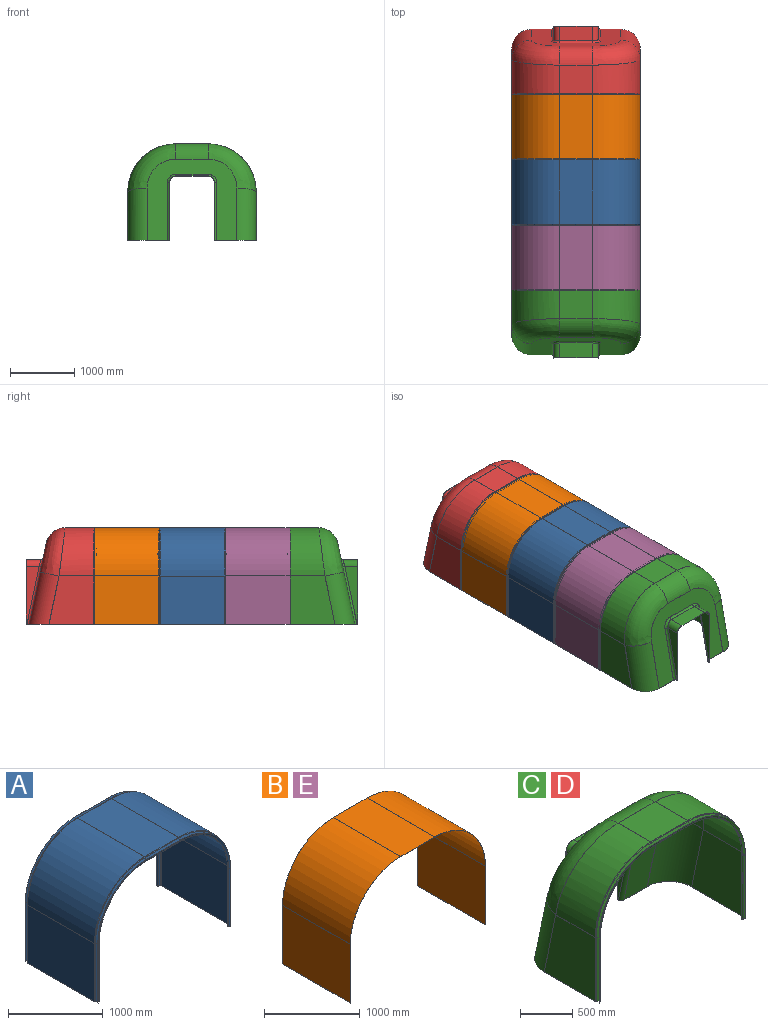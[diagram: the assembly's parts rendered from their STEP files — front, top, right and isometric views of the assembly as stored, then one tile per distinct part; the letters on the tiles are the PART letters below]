
ASSEMBLY  parts=5 mates=4
PART A: 102 faces, bbox 2123.6x1086.8x1561.8 mm
  f0: plane 1086.76x38mm, normal (0,0,-1), area 2320.8mm2, adj f3,f7,f12,f13,f14,f15,f16,f17
  f1: plane 1000x750mm, normal (-1,0,0), area 750000mm2, adj f2,f6,f52,f93
  f2: plane 1086.76x38mm, normal (0,0,-1), area 2320.8mm2, adj f1,f11,f48,f49,f50,f51,f52,f53
  f3: plane 1000x750mm, normal (1,0,0), area 750000mm2, adj f0,f5,f16,f57
  f4: plane 1000x500mm, normal (0,0,1), area 500000mm2, adj f5,f6,f34,f75
  f5: cylinder r=750mm len=1000mm, axis (0,1,0), area 1178097.2mm2, adj f3,f4,f25,f66
  f6: cylinder r=750mm len=1000mm, axis (0,-1,0), area 1178097.2mm2, adj f1,f4,f43,f84
  f7: plane 1000x750mm, normal (-1,0,0), area 750000mm2, adj f0,f8,f17,f65
  f8: cylinder r=748mm len=1000mm, axis (0,-1,0), area 1174955.7mm2, adj f7,f9,f26,f74
  f9: plane 1000x500mm, normal (0,0,-1), area 500000mm2, adj f8,f10,f35,f83
  f10: cylinder r=748mm len=1000mm, axis (0,-1,0), area 1174955.7mm2, adj f9,f11,f44,f92
  f11: plane 1000x750mm, normal (1,0,0), area 750000mm2, adj f2,f10,f53,f101
  f12: plane 750x1.84mm, normal (0.92,-0.39,0), area 1500mm2, adj f0,f13,f20,f21
  f13: plane 750x21.74mm, normal (0.39,0.92,0), area 17709.1mm2, adj f0,f12,f14,f22
  f14: cylinder r=7mm len=750mm, axis (0,0,1), area 12278.4mm2, adj f0,f13,f15,f23
  f15: plane 750x26.25mm, normal (0.39,-0.92,0), area 21389.1mm2, adj f0,f14,f16,f24
  f16: cylinder r=9mm len=750mm, axis (0,0,1), area 7893.3mm2, adj f0,f3,f15,f25
  f17: cylinder r=7mm len=750mm, axis (0,0,1), area 6139.2mm2, adj f0,f7,f18,f26
  f18: plane 750x26.25mm, normal (-0.39,0.92,0), area 21389.1mm2, adj f0,f17,f19,f27
  f19: cylinder r=9mm len=750mm, axis (0,0,1), area 15786.5mm2, adj f0,f18,f20,f28
  f20: plane 750x21.74mm, normal (-0.39,-0.92,0), area 17709.1mm2, adj f0,f12,f19,f29
  f21: cone r=739.22mm half-angle=23deg, axis (0,1,0), area 2323.6mm2, adj f12,f22,f29,f30
  f22: cone r=740mm half-angle=67deg, axis (0,-1,0), area 27043.5mm2, adj f13,f21,f23,f31
  f23: torus R=721mm, axis (0,-1,0), area 18399.4mm2, adj f14,f22,f24,f32
  f24: cone r=718.26mm half-angle=67deg, axis (0,1,0), area 32764.3mm2, adj f15,f23,f25,f33
  f25: torus R=741mm, axis (0,-1,0), area 12367mm2, adj f5,f16,f24,f34
  f26: torus R=741mm, axis (0,-1,0), area 9598.6mm2, adj f8,f17,f27,f35
  f27: cone r=743.74mm half-angle=67deg, axis (0,1,0), area 32729.3mm2, adj f18,f26,f28,f36
  f28: torus R=721mm, axis (0,-1,0), area 23604.3mm2, adj f19,f27,f29,f37
  f29: cone r=717.48mm half-angle=67deg, axis (0,-1,0), area 27014.5mm2, adj f20,f21,f28,f38
  f30: plane 500x1.84mm, normal (0,-0.39,0.92), area 1000mm2, adj f21,f31,f38,f39
  f31: plane 500x21.74mm, normal (0,0.92,0.39), area 11806.1mm2, adj f22,f30,f32,f40
  f32: cylinder r=7mm len=500mm, axis (-1,0,0), area 8185.6mm2, adj f23,f31,f33,f41
  f33: plane 500x26.25mm, normal (0,-0.92,0.39), area 14259.4mm2, adj f24,f32,f34,f42
  f34: cylinder r=9mm len=500mm, axis (-1,0,0), area 5262.2mm2, adj f4,f25,f33,f43
  f35: cylinder r=7mm len=500mm, axis (-1,0,0), area 4092.8mm2, adj f9,f26,f36,f44
  f36: plane 500x26.25mm, normal (0,0.92,-0.39), area 14259.4mm2, adj f27,f35,f37,f45
  f37: cylinder r=9mm len=500mm, axis (-1,0,0), area 10524.3mm2, adj f28,f36,f38,f46
  f38: plane 500x21.74mm, normal (0,-0.92,-0.39), area 11806.1mm2, adj f29,f30,f37,f47
  f39: cone r=739.22mm half-angle=23deg, axis (0,1,0), area 2323.6mm2, adj f30,f40,f47,f48
  f40: cone r=740mm half-angle=67deg, axis (0,-1,0), area 27043.5mm2, adj f31,f39,f41,f49
  f41: torus R=721mm, axis (0,-1,0), area 18399.4mm2, adj f32,f40,f42,f50
  f42: cone r=718.26mm half-angle=67deg, axis (0,1,0), area 32764.3mm2, adj f33,f41,f43,f51
  f43: torus R=741mm, axis (0,-1,0), area 12367mm2, adj f6,f34,f42,f52
  f44: torus R=741mm, axis (0,-1,0), area 9598.6mm2, adj f10,f35,f45,f53
  f45: cone r=743.74mm half-angle=67deg, axis (0,1,0), area 32729.3mm2, adj f36,f44,f46,f54
  f46: torus R=721mm, axis (0,-1,0), area 23604.3mm2, adj f37,f45,f47,f55
  f47: cone r=717.48mm half-angle=67deg, axis (0,-1,0), area 27014.5mm2, adj f38,f39,f46,f56
  f48: plane 750x1.84mm, normal (-0.92,-0.39,0), area 1500mm2, adj f2,f39,f49,f56
  f49: plane 750x21.74mm, normal (-0.39,0.92,0), area 17709.1mm2, adj f2,f40,f48,f50
  f50: cylinder r=7mm len=750mm, axis (0,0,-1), area 12278.4mm2, adj f2,f41,f49,f51
  f51: plane 750x26.25mm, normal (-0.39,-0.92,0), area 21389.1mm2, adj f2,f42,f50,f52
  f52: cylinder r=9mm len=750mm, axis (0,0,-1), area 7893.3mm2, adj f1,f2,f43,f51
  f53: cylinder r=7mm len=750mm, axis (0,0,-1), area 6139.2mm2, adj f2,f11,f44,f54
  f54: plane 750x26.25mm, normal (0.39,0.92,0), area 21389.1mm2, adj f2,f45,f53,f55
  f55: cylinder r=9mm len=750mm, axis (0,0,-1), area 15786.5mm2, adj f2,f46,f54,f56
  f56: plane 750x21.74mm, normal (0.39,-0.92,0), area 17709.1mm2, adj f2,f47,f48,f55
  f57: cylinder r=9mm len=750mm, axis (0,0,1), area 7893.3mm2, adj f0,f3,f58,f66
  f58: plane 750x26.25mm, normal (0.39,0.92,0), area 21389.1mm2, adj f0,f57,f59,f67
  f59: cylinder r=7mm len=750mm, axis (0,0,1), area 12278.4mm2, adj f0,f58,f60,f68
  f60: plane 750x21.74mm, normal (0.39,-0.92,0), area 17709.1mm2, adj f0,f59,f61,f69
  f61: plane 750x1.84mm, normal (0.92,0.39,0), area 1500mm2, adj f0,f60,f62,f70
  f62: plane 750x21.74mm, normal (-0.39,0.92,0), area 17709.1mm2, adj f0,f61,f63,f71
  f63: cylinder r=9mm len=750mm, axis (0,0,1), area 15786.5mm2, adj f0,f62,f64,f72
  f64: plane 750x26.25mm, normal (-0.39,-0.92,0), area 21389.1mm2, adj f0,f63,f65,f73
  f65: cylinder r=7mm len=750mm, axis (0,0,1), area 6139.2mm2, adj f0,f7,f64,f74
  f66: torus R=741mm, axis (0,-1,0), area 12367mm2, adj f5,f57,f67,f75
  f67: cone r=744.52mm half-angle=67deg, axis (0,-1,0), area 32764.3mm2, adj f58,f66,f68,f76
  f68: torus R=721mm, axis (0,-1,0), area 18399.4mm2, adj f59,f67,f69,f77
  f69: cone r=718.26mm half-angle=67deg, axis (0,1,0), area 27043.5mm2, adj f60,f68,f70,f78
  f70: cone r=740mm half-angle=23deg, axis (0,-1,0), area 2323.6mm2, adj f61,f69,f71,f79
  f71: cone r=739.22mm half-angle=67deg, axis (0,1,0), area 27014.5mm2, adj f62,f70,f72,f80
  f72: torus R=721mm, axis (0,-1,0), area 23604.3mm2, adj f63,f71,f73,f81
  f73: cone r=717.48mm half-angle=67deg, axis (0,-1,0), area 32729.3mm2, adj f64,f72,f74,f82
  f74: torus R=741mm, axis (0,-1,0), area 9598.6mm2, adj f8,f65,f73,f83
  f75: cylinder r=9mm len=500mm, axis (-1,0,0), area 5262.2mm2, adj f4,f66,f76,f84
  f76: plane 500x26.25mm, normal (0,0.92,0.39), area 14259.4mm2, adj f67,f75,f77,f85
  f77: cylinder r=7mm len=500mm, axis (-1,0,0), area 8185.6mm2, adj f68,f76,f78,f86
  f78: plane 500x21.74mm, normal (0,-0.92,0.39), area 11806.1mm2, adj f69,f77,f79,f87
  f79: plane 500x1.84mm, normal (0,0.39,0.92), area 1000mm2, adj f70,f78,f80,f88
  f80: plane 500x21.74mm, normal (0,0.92,-0.39), area 11806.1mm2, adj f71,f79,f81,f89
  f81: cylinder r=9mm len=500mm, axis (-1,0,0), area 10524.3mm2, adj f72,f80,f82,f90
  f82: plane 500x26.25mm, normal (0,-0.92,-0.39), area 14259.4mm2, adj f73,f81,f83,f91
  f83: cylinder r=7mm len=500mm, axis (-1,0,0), area 4092.8mm2, adj f9,f74,f82,f92
  f84: torus R=741mm, axis (0,-1,0), area 12367mm2, adj f6,f75,f85,f93
  f85: cone r=744.52mm half-angle=67deg, axis (0,-1,0), area 32764.3mm2, adj f76,f84,f86,f94
  f86: torus R=721mm, axis (0,-1,0), area 18399.4mm2, adj f77,f85,f87,f95
  f87: cone r=718.26mm half-angle=67deg, axis (0,1,0), area 27043.5mm2, adj f78,f86,f88,f96
  f88: cone r=740mm half-angle=23deg, axis (0,-1,0), area 2323.6mm2, adj f79,f87,f89,f97
  f89: cone r=739.22mm half-angle=67deg, axis (0,1,0), area 27014.5mm2, adj f80,f88,f90,f98
  f90: torus R=721mm, axis (0,-1,0), area 23604.3mm2, adj f81,f89,f91,f99
  f91: cone r=717.48mm half-angle=67deg, axis (0,-1,0), area 32729.3mm2, adj f82,f90,f92,f100
  f92: torus R=741mm, axis (0,-1,0), area 9598.6mm2, adj f10,f83,f91,f101
  f93: cylinder r=9mm len=750mm, axis (0,0,-1), area 7893.3mm2, adj f1,f2,f84,f94
  f94: plane 750x26.25mm, normal (-0.39,0.92,0), area 21389.1mm2, adj f2,f85,f93,f95
  f95: cylinder r=7mm len=750mm, axis (0,0,-1), area 12278.4mm2, adj f2,f86,f94,f96
  f96: plane 750x21.74mm, normal (-0.39,-0.92,0), area 17709.1mm2, adj f2,f87,f95,f97
  f97: plane 750x1.84mm, normal (-0.92,0.39,0), area 1500mm2, adj f2,f88,f96,f98
  f98: plane 750x21.74mm, normal (0.39,0.92,0), area 17709.1mm2, adj f2,f89,f97,f99
  f99: cylinder r=9mm len=750mm, axis (0,0,-1), area 15786.5mm2, adj f2,f90,f98,f100
  f100: plane 750x26.25mm, normal (0.39,-0.92,0), area 21389.1mm2, adj f2,f91,f99,f101
  f101: cylinder r=7mm len=750mm, axis (0,0,-1), area 6139.2mm2, adj f2,f11,f92,f100
PART B: 14 faces, bbox 2000x1000x1500 mm
  f0: plane 1000x2mm, normal (0,0,-1), area 2000mm2, adj f1,f5,f6,f9
  f1: plane 1000x750mm, normal (1,0,0), area 750000mm2, adj f0,f5,f6,f7
  f2: plane 1000x500mm, normal (0,0,1), area 500000mm2, adj f5,f6,f7,f8
  f3: plane 1000x750mm, normal (-1,0,0), area 750000mm2, adj f4,f5,f6,f8
  f4: plane 1000x2mm, normal (0,0,-1), area 2000mm2, adj f3,f5,f6,f13
  f5: plane 2000x1500mm, normal (0,-1,0), area 8706.1mm2, adj f0,f1,f2,f3,f4,f7,f8,f9
  f6: plane 2000x1500mm, normal (0,1,0), area 8706.1mm2, adj f0,f1,f2,f3,f4,f7,f8,f9
  f7: cylinder r=750mm len=1000mm, axis (0,1,0), area 1178097.2mm2, adj f1,f2,f5,f6
  f8: cylinder r=750mm len=1000mm, axis (0,1,0), area 1178097.2mm2, adj f2,f3,f5,f6
  f9: plane 1000x750mm, normal (-1,0,0), area 750000mm2, adj f0,f5,f6,f10
  f10: cylinder r=748mm len=1000mm, axis (0,-1,0), area 1174955.7mm2, adj f5,f6,f9,f11
  f11: plane 1000x500mm, normal (0,0,-1), area 500000mm2, adj f5,f6,f10,f12
  f12: cylinder r=748mm len=1000mm, axis (0,-1,0), area 1174955.7mm2, adj f5,f6,f11,f13
  f13: plane 1000x750mm, normal (1,0,0), area 750000mm2, adj f4,f5,f6,f12
PART C: 96 faces, bbox 2123.6x1093x1623.6 mm
  f0: plane 1092.95x652mm, normal (0,0,-1), area 3568.5mm2, adj f4,f7,f12,f15,f16,f19,f26,f37
  f1: plane 1092.95x652mm, normal (0,0,-1), area 3568.5mm2, adj f2,f7,f8,f14,f16,f21,f24,f36
  f2: plane 750x693.42mm, normal (1,0,0), area 460843.6mm2, adj f1,f5,f8,f55
  f3: plane 500x440.74mm, normal (0,0,1), area 220369.6mm2, adj f5,f6,f10,f73
  f4: plane 750x693.42mm, normal (-1,0,0), area 460843.6mm2, adj f0,f6,f12,f91
  f5: cylinder r=750mm len=750mm, axis (0,-1,0), area 559798.4mm2, adj f2,f3,f9,f64
  f6: cylinder r=750mm len=750mm, axis (0,1,0), area 559798.4mm2, adj f3,f4,f11,f82
  f7: plane 1400x1261.82mm, normal (0,0.98,0.21), area 915702.1mm2, adj f0,f1,f8,f9,f10,f11,f12,f19
  f8: cylinder r=300mm len=873.63mm, axis (0,-0.21,0.98), area 380130.7mm2, adj f1,f2,f7,f9
  f9: bspline ~815.38x752.58mm, area 431302.8mm2, adj f5,f7,f8,f10
  f10: cylinder r=300mm len=500mm, axis (-1,0,0), area 204489mm2, adj f3,f7,f9,f11
  f11: bspline ~817.96x815.38mm, area 431302.8mm2, adj f6,f7,f10,f12
  f12: cylinder r=300mm len=873.63mm, axis (0,0.21,-0.98), area 380130.7mm2, adj f0,f4,f7,f11
  f13: plane 500x232.17mm, normal (0,0,1), area 116085.4mm2, adj f16,f17,f18,f22
  f14: plane 900x203.74mm, normal (1,0,0), area 98089.4mm2, adj f1,f16,f18,f21
  f15: plane 900x203.74mm, normal (-1,0,0), area 98089.4mm2, adj f0,f16,f17,f19
  f16: plane 1000x700mm, normal (0,1,0), area 5222mm2, adj f0,f1,f13,f14,f15,f17,f18,f35
  f17: cylinder r=100mm len=232.17mm, axis (0,-1,0), area 34846.7mm2, adj f13,f15,f16,f20
  f18: cylinder r=100mm len=232.17mm, axis (0,1,0), area 34846.7mm2, adj f13,f14,f16,f23
  f19: cylinder r=35mm len=907.21mm, axis (0,0.21,-0.98), area 50307.2mm2, adj f0,f7,f15,f20
  f20: bspline ~146.77x135mm, area 9131.3mm2, adj f7,f17,f19,f22
  f21: cylinder r=35mm len=907.21mm, axis (0,-0.21,0.98), area 50307.2mm2, adj f1,f7,f14,f23
  f22: cylinder r=35mm len=500mm, axis (-1,0,0), area 23857mm2, adj f7,f13,f20,f23
  f23: bspline ~146.77x146.77mm, area 9131.3mm2, adj f7,f18,f21,f22
  f24: plane 750x693mm, normal (-1,0,0), area 460843.2mm2, adj f1,f27,f30,f45,f56
  f25: plane 500x440.74mm, normal (0,0,-1), area 220369.6mm2, adj f27,f28,f32,f74
  f26: plane 750x693mm, normal (1,0,0), area 460843.2mm2, adj f0,f28,f34,f49,f92
  f27: cylinder r=748mm len=748mm, axis (0,-1,0), area 558305.6mm2, adj f24,f25,f31,f65
  f28: cylinder r=748mm len=748mm, axis (0,1,0), area 558305.6mm2, adj f25,f26,f33,f83
  f29: plane 1400x1259.4mm, normal (0,-0.98,-0.21), area 914149.1mm2, adj f30,f31,f32,f33,f34,f40,f41,f42
  f30: cylinder r=298mm len=870.81mm, axis (0,-0.21,0.98), area 376514.3mm2, adj f24,f29,f31,f45
  f31: bspline ~813.21x750.55mm, area 427614.9mm2, adj f27,f29,f30,f32
  f32: cylinder r=298mm len=500mm, axis (-1,0,0), area 203125.7mm2, adj f25,f29,f31,f33
  f33: bspline ~815.76x813.21mm, area 427614.9mm2, adj f28,f29,f32,f34
  f34: cylinder r=298mm len=870.81mm, axis (0,0.21,-0.98), area 376514.3mm2, adj f26,f29,f33,f49
  f35: plane 500x232.17mm, normal (0,0,-1), area 116085.4mm2, adj f16,f38,f39,f43
  f36: plane 900x203.74mm, normal (-1,0,0), area 98089.8mm2, adj f1,f16,f39,f42,f47
  f37: plane 900x203.74mm, normal (1,0,0), area 98089.8mm2, adj f0,f16,f38,f40,f50
  f38: cylinder r=98mm len=232.17mm, axis (0,-1,0), area 34149.8mm2, adj f16,f35,f37,f41
  f39: cylinder r=98mm len=232.17mm, axis (0,1,0), area 34149.8mm2, adj f16,f35,f36,f44
  f40: cylinder r=37mm len=905.62mm, axis (0,0.21,-0.98), area 53047.5mm2, adj f29,f37,f41,f50
  f41: bspline ~146.77x135mm, area 9552.2mm2, adj f29,f38,f40,f43
  f42: cylinder r=37mm len=905.62mm, axis (0,-0.21,0.98), area 53047.5mm2, adj f29,f36,f44,f47
  f43: cylinder r=37mm len=500mm, axis (-1,0,0), area 25220.3mm2, adj f29,f35,f41,f44
  f44: bspline ~135x135mm, area 9552.2mm2, adj f29,f39,f42,f43
  f45: extruded ~304.54x298mm, area 946.5mm2, adj f1,f24,f30,f46
  f46: plane 315x2mm, normal (0,-1,0), area 630mm2, adj f1,f29,f45,f47
  f47: extruded ~37.81x37mm, area 117.5mm2, adj f1,f36,f42,f46
  f48: plane 315x2mm, normal (0,-1,0), area 630mm2, adj f0,f29,f49,f50
  f49: extruded ~304.54x298mm, area 946.5mm2, adj f0,f26,f34,f48
  f50: extruded ~37.81x37mm, area 117.5mm2, adj f0,f37,f40,f48
  f51: plane 750x1.85mm, normal (0.93,-0.37,0), area 1500mm2, adj f1,f52,f59,f60
  f52: plane 750x21.62mm, normal (0.37,0.93,0), area 17490.3mm2, adj f1,f51,f53,f61
  f53: cylinder r=7mm len=750mm, axis (0,0,1), area 12370mm2, adj f1,f52,f54,f62
  f54: plane 750x26.25mm, normal (0.39,-0.92,0), area 21389.1mm2, adj f1,f53,f55,f63
  f55: cylinder r=9mm len=750mm, axis (0,0,1), area 7893.3mm2, adj f1,f2,f54,f64
  f56: cylinder r=7mm len=750mm, axis (0,0,1), area 6139.2mm2, adj f1,f24,f57,f65
  f57: plane 750x26.25mm, normal (-0.39,0.92,0), area 21389.1mm2, adj f1,f56,f58,f66
  f58: cylinder r=9mm len=750mm, axis (0,0,1), area 15904.3mm2, adj f1,f57,f59,f67
  f59: plane 750x21.62mm, normal (-0.37,-0.93,0), area 17490.3mm2, adj f1,f51,f58,f68
  f60: cone r=739.25mm half-angle=22deg, axis (0,1,0), area 2323.6mm2, adj f51,f61,f68,f69
  f61: cone r=740mm half-angle=68deg, axis (0,-1,0), area 26711.3mm2, adj f52,f60,f62,f70
  f62: torus R=721mm, axis (0,-1,0), area 18537.2mm2, adj f53,f61,f63,f71
  f63: cone r=718.26mm half-angle=67deg, axis (0,1,0), area 32764.3mm2, adj f54,f62,f64,f72
  f64: torus R=741mm, axis (0,-1,0), area 12367mm2, adj f5,f55,f63,f73
  f65: torus R=741mm, axis (0,-1,0), area 9598.6mm2, adj f27,f56,f66,f74
  f66: cone r=743.74mm half-angle=67deg, axis (0,1,0), area 32729.3mm2, adj f57,f65,f67,f75
  f67: torus R=721mm, axis (0,-1,0), area 23781.4mm2, adj f58,f66,f68,f76
  f68: cone r=717.63mm half-angle=68deg, axis (0,-1,0), area 26683.8mm2, adj f59,f60,f67,f77
  f69: plane 500x1.85mm, normal (0,-0.37,0.93), area 1000mm2, adj f60,f70,f77,f78
  f70: plane 500x21.62mm, normal (0,0.93,0.37), area 11660.2mm2, adj f61,f69,f71,f79
  f71: cylinder r=7mm len=500mm, axis (-1,0,0), area 8246.7mm2, adj f62,f70,f72,f80
  f72: plane 500x26.25mm, normal (0,-0.92,0.39), area 14259.4mm2, adj f63,f71,f73,f81
  f73: cylinder r=9mm len=500mm, axis (-1,0,0), area 5262.2mm2, adj f3,f64,f72,f82
  f74: cylinder r=7mm len=500mm, axis (-1,0,0), area 4092.8mm2, adj f25,f65,f75,f83
  f75: plane 500x26.25mm, normal (0,0.92,-0.39), area 14259.4mm2, adj f66,f74,f76,f84
  f76: cylinder r=9mm len=500mm, axis (-1,0,0), area 10602.9mm2, adj f67,f75,f77,f85
  f77: plane 500x21.62mm, normal (0,-0.93,-0.37), area 11660.2mm2, adj f68,f69,f76,f86
  f78: cone r=739.25mm half-angle=22deg, axis (0,1,0), area 2323.6mm2, adj f69,f79,f86,f87
  f79: cone r=740mm half-angle=68deg, axis (0,-1,0), area 26711.3mm2, adj f70,f78,f80,f88
  f80: torus R=721mm, axis (0,-1,0), area 18537.2mm2, adj f71,f79,f81,f89
  f81: cone r=718.26mm half-angle=67deg, axis (0,1,0), area 32764.3mm2, adj f72,f80,f82,f90
  f82: torus R=741mm, axis (0,-1,0), area 12367mm2, adj f6,f73,f81,f91
  f83: torus R=741mm, axis (0,-1,0), area 9598.6mm2, adj f28,f74,f84,f92
  f84: cone r=743.74mm half-angle=67deg, axis (0,1,0), area 32729.3mm2, adj f75,f83,f85,f93
  f85: torus R=721mm, axis (0,-1,0), area 23781.4mm2, adj f76,f84,f86,f94
  f86: cone r=717.63mm half-angle=68deg, axis (0,-1,0), area 26683.8mm2, adj f77,f78,f85,f95
  f87: plane 750x1.85mm, normal (-0.93,-0.37,0), area 1500mm2, adj f0,f78,f88,f95
  f88: plane 750x21.62mm, normal (-0.37,0.93,0), area 17490.3mm2, adj f0,f79,f87,f89
  f89: cylinder r=7mm len=750mm, axis (0,0,-1), area 12370mm2, adj f0,f80,f88,f90
  f90: plane 750x26.25mm, normal (-0.39,-0.92,0), area 21389.1mm2, adj f0,f81,f89,f91
  f91: cylinder r=9mm len=750mm, axis (0,0,-1), area 7893.3mm2, adj f0,f4,f82,f90
  f92: cylinder r=7mm len=750mm, axis (0,0,-1), area 6139.2mm2, adj f0,f26,f83,f93
  f93: plane 750x26.25mm, normal (0.39,0.92,0), area 21389.1mm2, adj f0,f84,f92,f94
  f94: cylinder r=9mm len=750mm, axis (0,0,-1), area 15904.3mm2, adj f0,f85,f93,f95
  f95: plane 750x21.62mm, normal (0.37,-0.93,0), area 17490.3mm2, adj f0,f86,f87,f94
PART D: same geometry as C
PART E: same geometry as B
PLACE A t=(-404.9,136.97,55.65)mm
PLACE B t=(-404.9,1155.15,56)mm
PLACE C rot(axis=(0,0,1),180deg) t=(-404.9,-1396.03,56.07)mm
PLACE D t=(-404.9,1673.57,56.28)mm
PLACE E t=(-404.9,-887.95,56.07)mm
MATE planar D.f2 <-> A.f3  axis (1,0,0) through (595.1,1982.49,415.22)mm
MATE planar C.f4 <-> A.f3  axis (1,0,0) through (595.1,-1704.95,415.01)mm
MATE planar C.f4 <-> E.f1  axis (1,0,0) through (595.1,-1704.95,415.01)mm
MATE planar D.f2 <-> B.f1  axis (1,0,0) through (595.1,1982.49,415.22)mm
